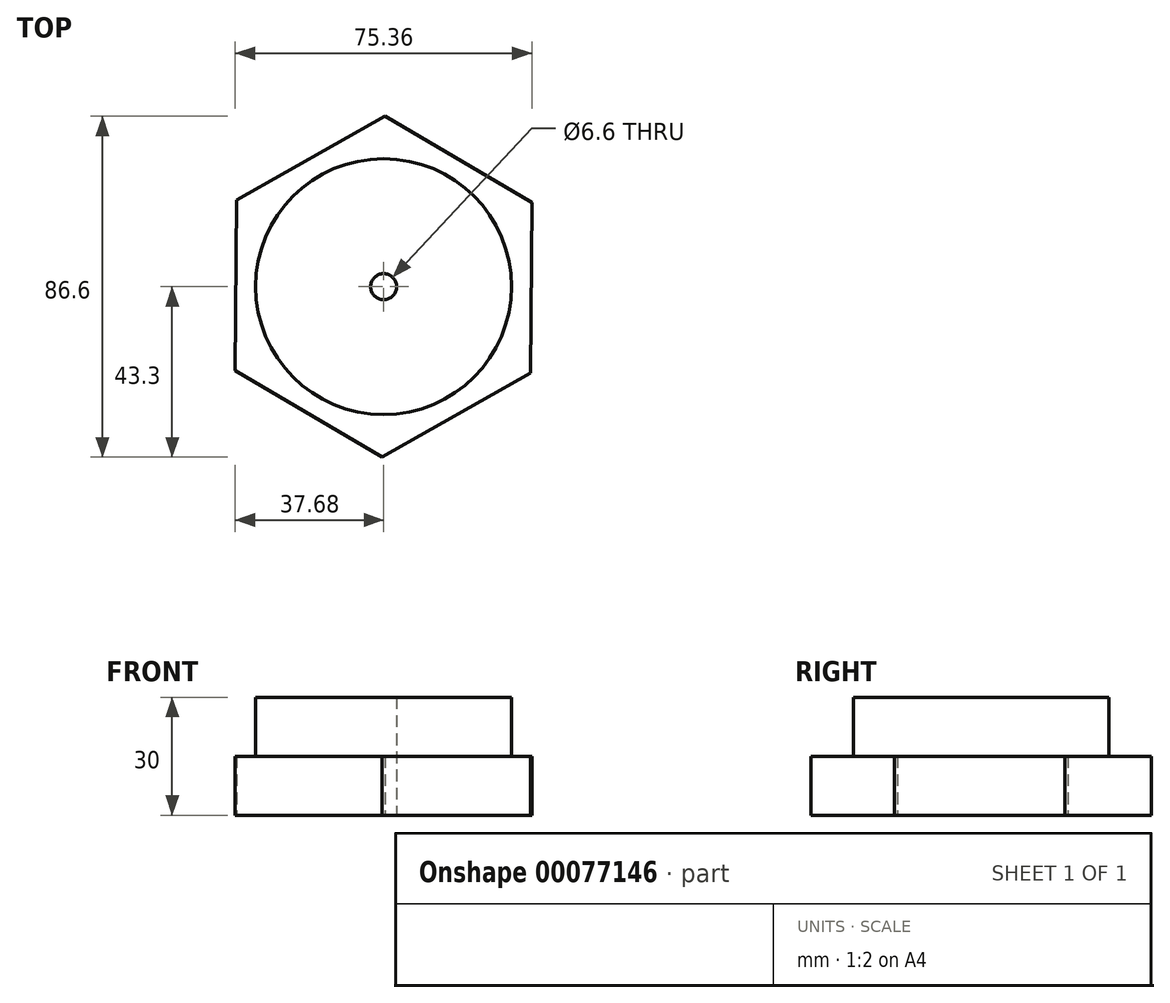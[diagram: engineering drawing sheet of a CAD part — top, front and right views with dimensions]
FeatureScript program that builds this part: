
annotation { "Feature Type Name" : "Feature", "Feature Type Description" : "" }
export const myFeature = defineFeature(function(context is Context, id is Id, definition is map)
    precondition{}
    {
        {
            var Q0;
            Q0=qCreatedBy(makeId("Top.planeOp"),FACE);
            var sketch = newSketch(context, id + "F0", { "sketchPlane" : qUnion([Q0])});
            skCircle(sketch, "E0.cCircle", {"center": v(0, 0) * mm, "radius": 37.5 * mm, "construction": true});
            skLineSegment(sketch, "E0.0", {"start": v(-37.31, 21.97) * mm, "end": v(0.37, 43.3) * mm});
            skLineSegment(sketch, "E0.1", {"start": v(0.37, 43.3) * mm, "end": v(37.68, 21.33) * mm});
            skLineSegment(sketch, "E0.2", {"start": v(37.68, 21.33) * mm, "end": v(37.31, -21.97) * mm});
            skLineSegment(sketch, "E0.3", {"start": v(37.31, -21.97) * mm, "end": v(-0.37, -43.3) * mm});
            skLineSegment(sketch, "E0.4", {"start": v(-0.37, -43.3) * mm, "end": v(-37.68, -21.33) * mm});
            skLineSegment(sketch, "E0.5", {"start": v(-37.68, -21.33) * mm, "end": v(-37.31, 21.97) * mm});
            skPoint(sketch, "E0.0.midPoint", {"position": v(-18.47, 32.63) * mm});
            skSolve(sketch);
        }
        {
            var Q0;
            Q0=makeQuery(id+"F0.imprint","IMPRINT",FACE,{"disambiguationData":[TD([[makeQuery(id+"F0.imprint","IMPRINT",EDGE,{"derivedFrom":sQuery(id+"F0.wireOp",EDGE,"86af564a-6f25-41c4-9303-4fb3b4f97ad8.0")}),-1.0]])]});
            var Q1;
            Q1=makeQuery(id+"F0.imprint","IMPRINT",FACE,{"disambiguationData":[TD([[makeQuery(id+"F0.imprint","IMPRINT",EDGE,{"derivedFrom":sQuery(id+"F0.wireOp",EDGE,"E0.0")}),-1.0]])]});
            extrude(context, id + "F1", {"entities" : qUnion([Q0, Q1]), "depth" : 15 * mm});
        }
        {
            var Q0;
            Q0=makeQuery(id+"F1.opExtrude","CAP_FACE",FACE,{"disambiguationData":[OSD([sQuery(id+"F0.wireOp",EDGE,"E0.0"),sQuery(id+"F0.wireOp",EDGE,"E0.1"),sQuery(id+"F0.wireOp",EDGE,"E0.2"),sQuery(id+"F0.wireOp",EDGE,"E0.3"),sQuery(id+"F0.wireOp",EDGE,"E0.4"),sQuery(id+"F0.wireOp",EDGE,"E0.5")])],"isStart":false});
            var sketch = newSketch(context, id + "F2", { "sketchPlane" : qUnion([Q0])});
            skCircle(sketch, "E1", {"center": v(0, 0) * mm, "radius": 32.5 * mm});
            skCircle(sketch, "E2", {"center": v(0, 0) * mm, "radius": 32.67 * mm});
            skSolve(sketch);
        }
        {
            var Q0;
            Q0=makeQuery(id+"F2.imprint","IMPRINT",FACE,{"disambiguationData":[TD([[makeQuery(id+"F2.imprint","IMPRINT",EDGE,{"derivedFrom":sQuery(id+"F2.wireOp",EDGE,"E1")}),1.0]])]});
            extrude(context, id + "F3", {"entities" : qUnion([Q0]), "operationType" : NewBodyOperationType.ADD, "depth" : 15 * mm});
        }
        {
            var Q0;
            Q0=qCreatedBy(makeId("Top.planeOp"),FACE);
            var sketch = newSketch(context, id + "F4", { "sketchPlane" : qUnion([Q0])});
            skCircle(sketch, "E3", {"center": v(0, 0) * mm, "radius": 3.3 * mm});
            skSolve(sketch);
        }
        {
            var Q0;
            Q0 = qSketchRegion(id + "F4", true);
            extrude(context, id + "F5", {"entities" : qUnion([Q0]), "depth" : 30 * mm});
        }
        {
            var Q0;
            Q0=makeQuery(id+"F5.opExtrude","SWEPT_BODY",BODY,{"disambiguationData":[OSD([sQuery(id+"F4.wireOp",EDGE,"E3")])]});
            var Q1;
            Q1=makeQuery(id+"F1.opExtrude","SWEPT_BODY",BODY,{"disambiguationData":[OSD([sQuery(id+"F0.wireOp",EDGE,"E0.0"),sQuery(id+"F0.wireOp",EDGE,"E0.1"),sQuery(id+"F0.wireOp",EDGE,"E0.2"),sQuery(id+"F0.wireOp",EDGE,"E0.3"),sQuery(id+"F0.wireOp",EDGE,"E0.4"),sQuery(id+"F0.wireOp",EDGE,"E0.5")])]});
            booleanBodies(context, id + "F6", {"operationType" : BooleanOperationType.SUBTRACTION, "tools" : qUnion([Q0]), "targets" : qUnion([Q1])});
        }
    });
